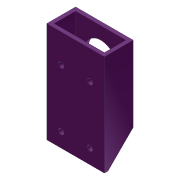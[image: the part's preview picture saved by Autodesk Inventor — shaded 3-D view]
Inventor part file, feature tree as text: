
AUTODESK INVENTOR PART (.ipt)
format: ipt  version: 2012 (Build 160160000, 160)  size: 120,320 bytes
history: native  units: in
note: dims shown in document units (in); Inventor stores cm internally (conversion verified against a paired STEP export)
features: extrude x4, sketch x4, shell x1
ambient origin geometry x8: Origin, YZ Plane, XZ Plane, XY Plane, X Axis, Y Axis, Z Axis, Center Point
bodies: Solid1 (feature_tree)
feature tree (9):
  extrude  "Extrusion1"  Depth=3.5in
  shell  "Shell1"  Thickness=1.0in
  extrude  "Extrusion2"  Depth=2.0in
  extrude  "Extrusion3"  Depth=0.5in
  extrude  "Extrusion5"  Depth=1.0in TaperAngle=0.0deg
  sketch  "Sketch1"  dims[d0=2.0in d1=3.5in d2=1.0in d3=0.0in]
  sketch  "Sketch2"  dims[d4=0.125in d5=2.0in]
  sketch  "Sketch3"  dims[d6=1.0in d7=0.5in]
  sketch  "Sketch5"  dims[d8=0.192in d9=1.0in d10=0.0in d11=0.875in d12=0.875in d13=1.0in d14=0.0in d19=2.5in d20=1.125in d21=1.0in d22=1.0in d23=0.0in]
